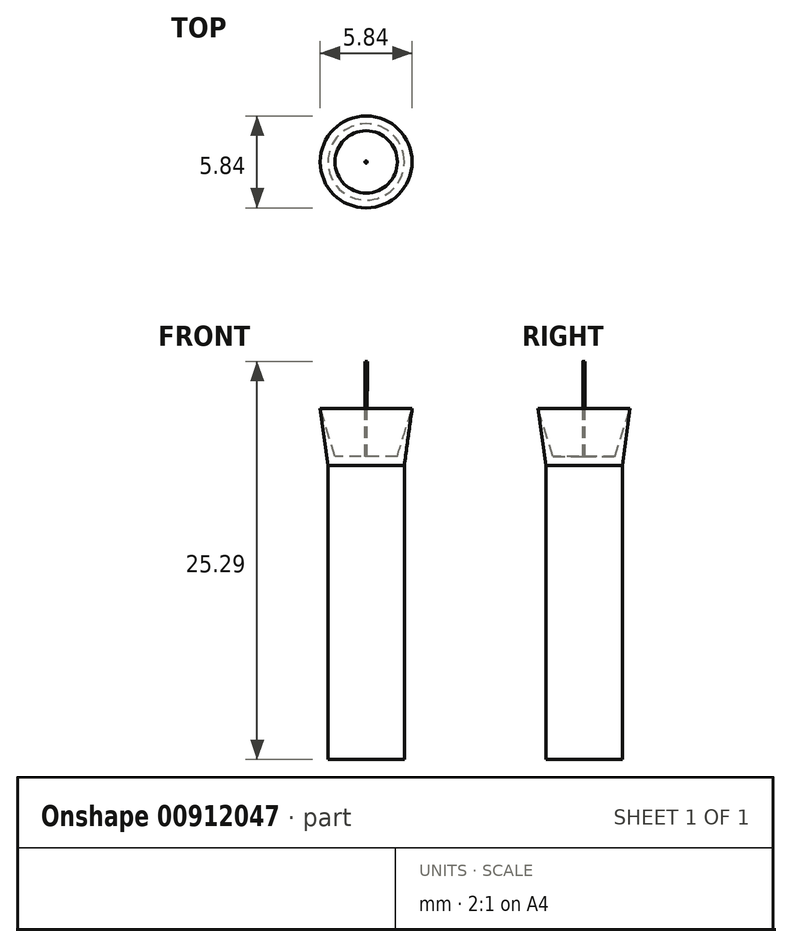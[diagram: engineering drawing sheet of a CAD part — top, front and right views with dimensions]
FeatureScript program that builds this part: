
annotation { "Feature Type Name" : "Feature", "Feature Type Description" : "" }
export const myFeature = defineFeature(function(context is Context, id is Id, definition is map)
    precondition{}
    {
        {
            var Q0;
            Q0=qCreatedBy(makeId("Front.planeOp"),FACE);
            var sketch = newSketch(context, id + "F0", { "sketchPlane" : qUnion([Q0])});
            skLineSegment(sketch, "E0", {"start": v(0, 40.72) * mm, "end": v(0, -28.06) * mm});
            skLineSegment(sketch, "E1", {"start": v(0, -28.06) * mm, "end": v(8.92, -28.06) * mm});
            skLineSegment(sketch, "E2", {"start": v(0, 40.72) * mm, "end": v(8.92, 40.72) * mm});
            skLineSegment(sketch, "E3", {"start": v(8.92, -28.06) * mm, "end": v(8.92, 40.72) * mm});
            skLineSegment(sketch, "E4", {"start": v(8.92, 40.72) * mm, "end": v(10.74, 54) * mm});
            skLineSegment(sketch, "E5", {"start": v(0, 42.86) * mm, "end": v(0, 40.72) * mm});
            skLineSegment(sketch, "E6", {"start": v(2.3, 42.86) * mm, "end": v(7.28, 42.86) * mm});
            skLineSegment(sketch, "E7", {"start": v(7.28, 42.86) * mm, "end": v(10.74, 54) * mm});
            skLineSegment(sketch, "E8", {"start": v(10.74, 54) * mm, "end": v(7.28, 42.86) * mm});
            skLineSegment(sketch, "E9.bottom", {"start": v(0, 42.86) * mm, "end": v(0, 42.86) * mm});
            skLineSegment(sketch, "E9.left", {"start": v(0, 42.86) * mm, "end": v(0, 42.86) * mm});
            skLineSegment(sketch, "E9.right", {"start": v(0, 42.86) * mm, "end": v(2.3, 42.86) * mm});
            skPoint(sketch, "E10.endSnap0", {"position": v(9.83, 47.37) * mm});
            skLineSegment(sketch, "E11.bottom", {"start": v(9.38, 49.62) * mm, "end": v(7.97, 49.62) * mm});
            skLineSegment(sketch, "E11.top", {"start": v(9.38, 49.96) * mm, "end": v(7.97, 49.96) * mm});
            skLineSegment(sketch, "E11.right", {"start": v(7.97, 49.62) * mm, "end": v(7.97, 49.96) * mm});
            skLineSegment(sketch, "E12", {"start": v(9.38, 49.96) * mm, "end": v(9.48, 49.96) * mm});
            skSolve(sketch);
        }
        {
            var Q0;
            Q0=makeQuery(id+"F0.imprint","IMPRINT",FACE,{"disambiguationData":[TD([[makeQuery(id+"F0.imprint","IMPRINT",EDGE,{"derivedFrom":sQuery(id+"F0.wireOp",EDGE,"E2")}),1.0]])]});
            var Q1;
            Q1=makeQuery(id+"F0.imprint","IMPRINT",FACE,{"disambiguationData":[TD([[makeQuery(id+"F0.imprint","IMPRINT",EDGE,{"derivedFrom":sQuery(id+"F0.wireOp",EDGE,"E0")}),1.0]])]});
            var Q2;
            Q2=sQuery(id+"F0.wireOp",EDGE,"E5");
            revolve(context, id + "F1", {"surfaceOperationType" : NewSurfaceOperationType.NEW, "entities" : qUnion([Q0, Q1]), "axis" : qUnion([Q2]), "revolveType" : RevolveType.FULL});
        }
        {
            var Q0;
            Q0=qCreatedBy(makeId("Top.planeOp"),FACE);
            cPlane(context, id + "F2", {"entities" : qUnion([Q0]), "cplaneType" : CPlaneType.OFFSET, "offset" : 65.02 * mm, "width" : 152.4 * mm, "height" : 152.4 * mm});
        }
        {
            var Q0;
            Q0=qCreatedBy(id+"F2.planeOp",FACE);
            var sketch = newSketch(context, id + "F3", { "sketchPlane" : qUnion([Q0])});
            skCircle(sketch, "E13", {"center": v(0, 0) * mm, "radius": 0.26 * mm});
            skSolve(sketch);
        }
        {
            var Q0;
            Q0=qCreatedBy(id+"F2.planeOp",FACE);
            cPlane(context, id + "F4", {"entities" : qUnion([Q0]), "cplaneType" : CPlaneType.OFFSET, "offset" : 22.17 * mm, "oppositeDirection" : true, "width" : 152.4 * mm, "height" : 152.4 * mm});
        }
        {
            var Q0;
            Q0=qCreatedBy(id+"F4.planeOp",FACE);
            var sketch = newSketch(context, id + "F5", { "sketchPlane" : qUnion([Q0])});
            skCircle(sketch, "E14", {"center": v(0, 0) * mm, "radius": 0.26 * mm});
            skSolve(sketch);
        }
        {
            var Q1;
            Q1=makeQuery(id+"F5.imprint","IMPRINT",FACE,{"disambiguationData":[TD([[makeQuery(id+"F5.imprint","IMPRINT",EDGE,{"derivedFrom":sQuery(id+"F5.wireOp",EDGE,"E14")}),1.0]])]});
            var Q2;
            Q2=makeQuery(id+"F3.imprint","IMPRINT",FACE,{"disambiguationData":[TD([[makeQuery(id+"F3.imprint","IMPRINT",EDGE,{"derivedFrom":sQuery(id+"F3.wireOp",EDGE,"E13")}),1.0]])]});
            loft(context, id + "F6", {"operationType" : NewBodyOperationType.ADD, "sheetProfilesArray" : [{ "sheetProfileEntities" : qUnion([Q1]) }, { "sheetProfileEntities" : qUnion([Q2]) }]});
        }
        {
            var Q0;
            Q0=makeQuery(id+"F1.opRevolve","SWEPT_BODY",BODY,{"disambiguationData":[OSD([sQuery(id+"F0.wireOp",EDGE,"E0"),sQuery(id+"F0.wireOp",EDGE,"E1"),sQuery(id+"F0.wireOp",EDGE,"E3"),sQuery(id+"F0.wireOp",EDGE,"E4"),sQuery(id+"F0.wireOp",EDGE,"E5"),sQuery(id+"F0.wireOp",EDGE,"E6"),sQuery(id+"F0.wireOp",EDGE,"E8"),sQuery(id+"F0.wireOp",EDGE,"E9.right")])]});
            var Q1;
            Q1=qCreatedBy(makeId("Origin.pointOp"),VERTEX);
            var Q2;
            Q2=qCreatedBy(makeId("Origin.pointOp"),VERTEX);
            transform(context, id + "F7", {"entities" : qUnion([Q0]), "transformType" : TransformType.SCALE_UNIFORMLY, "scale" : .2717, "scalePoint" : qUnion([Q2]), "makeCopy" : false});
        }
    });
